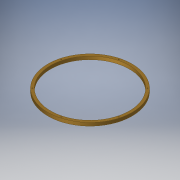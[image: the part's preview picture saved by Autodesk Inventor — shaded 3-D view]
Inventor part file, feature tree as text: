
AUTODESK INVENTOR PART (.ipt)
format: ipt  version: 2018 (Build 220112000, 112)  size: 121,856 bytes
history: native  units: in
note: dims shown in document units (in); Inventor stores cm internally (conversion verified against a paired STEP export)
features: sketch x2, extrude x1, hole x1, pattern_circular x1
ambient origin geometry x8: Origin, YZ Plane, XZ Plane, XY Plane, X Axis, Y Axis, Z Axis, Center Point
bodies: Solid1 (feature_tree)
feature tree (5):
  extrude  "Extrusion1"  Depth=7.5in
  hole  "Hole1"  [1 undecoded]
  pattern_circular  "Circular Pattern1"  Angle=45.0deg  [1 undecoded]
  sketch  "Sketch1"  dims[d0=8.0in d1=7.5in]
  sketch  "Sketch2"  dims[d2=0.3in d3=0.0in d4=3.875in d5=45.0deg d6=0.089in d7=0.224in d8=0.375in d9=0.25in d10=0.5635in d11=0.328in d12=0.8108in d13=2.3622in d14=360.0deg]
note: 2 required parameter values undecoded (feature->parameter linkage not recoverable at this tier; creation-order binding heuristic only, values carry confidence <= 0.55)
